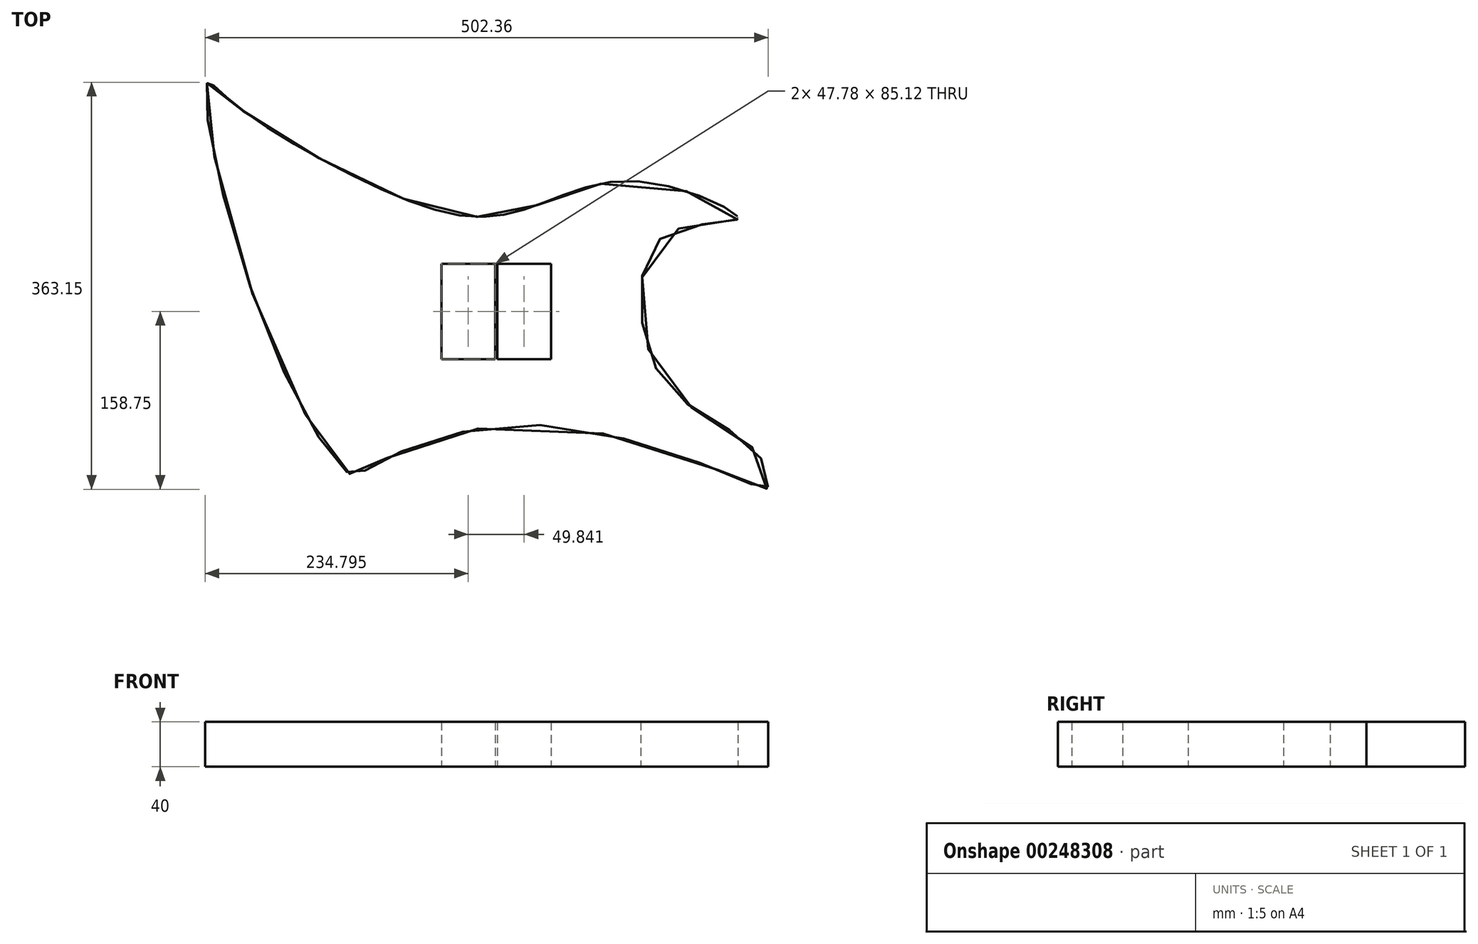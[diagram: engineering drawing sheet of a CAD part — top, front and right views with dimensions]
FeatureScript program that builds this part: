
annotation { "Feature Type Name" : "Feature", "Feature Type Description" : "" }
export const myFeature = defineFeature(function(context is Context, id is Id, definition is map)
    precondition{}
    {
        {
            var Q0;
            Q0=qCreatedBy(makeId("Top.planeOp"),FACE);
            var sketch = newSketch(context, id + "F0", { "sketchPlane" : qUnion([Q0])});
            skFitSpline(sketch, "E0", {"points": [v(-177.88, 206.8) * mm, v(-130.23, 0) * mm, v(-49.23, -142.5) * mm, v(-34.42, -137.26) * mm, v(114.53, -98.01) * mm, v(313.12, -153.2) * mm, v(322.12, -154.55) * mm, v(312.9, -122.92) * mm, v(239.08, -69.78) * mm, v(209.14, 13.74) * mm, v(237.15, 74.81) * mm, v(295.8, 85.84) * mm, v(215.19, 118.38) * mm, v(125.7, 101.37) * mm, v(61.42, 87.46) * mm, v(-49.31, 125) * mm, v(-161.07, 194.67) * mm, v(-177.88, 206.8) * mm]});
            skLineSegment(sketch, "E1", {"start": v(-187.9, 0) * mm, "end": v(299.03, 0) * mm, "construction": true});
            skPoint(sketch, "E2", {"position": v(209.77, 0) * mm});
            skLineSegment(sketch, "E3.bottom", {"start": v(81.36, 45.63) * mm, "end": v(129.14, 45.63) * mm});
            skLineSegment(sketch, "E3.top", {"start": v(81.36, -39.49) * mm, "end": v(129.14, -39.49) * mm});
            skLineSegment(sketch, "E3.left", {"start": v(81.36, 45.63) * mm, "end": v(81.36, -39.49) * mm});
            skLineSegment(sketch, "E3.right", {"start": v(129.14, 45.63) * mm, "end": v(129.14, -39.49) * mm});
            skLineSegment(sketch, "E4.bottom", {"start": v(31.52, 45.63) * mm, "end": v(79.3, 45.63) * mm});
            skLineSegment(sketch, "E4.top", {"start": v(31.52, -39.49) * mm, "end": v(79.3, -39.49) * mm});
            skLineSegment(sketch, "E4.left", {"start": v(31.52, 45.63) * mm, "end": v(31.52, -39.49) * mm});
            skLineSegment(sketch, "E4.right", {"start": v(79.3, 45.63) * mm, "end": v(79.3, -39.49) * mm});
            skSolve(sketch);
        }
        {
            var Q0;
            Q0 = qSketchRegion(id + "F0", true);
            extrude(context, id + "F1", {"entities" : qUnion([Q0]), "depth" : 40 * mm, "offsetDistance" : 25 * mm});
        }
    });
